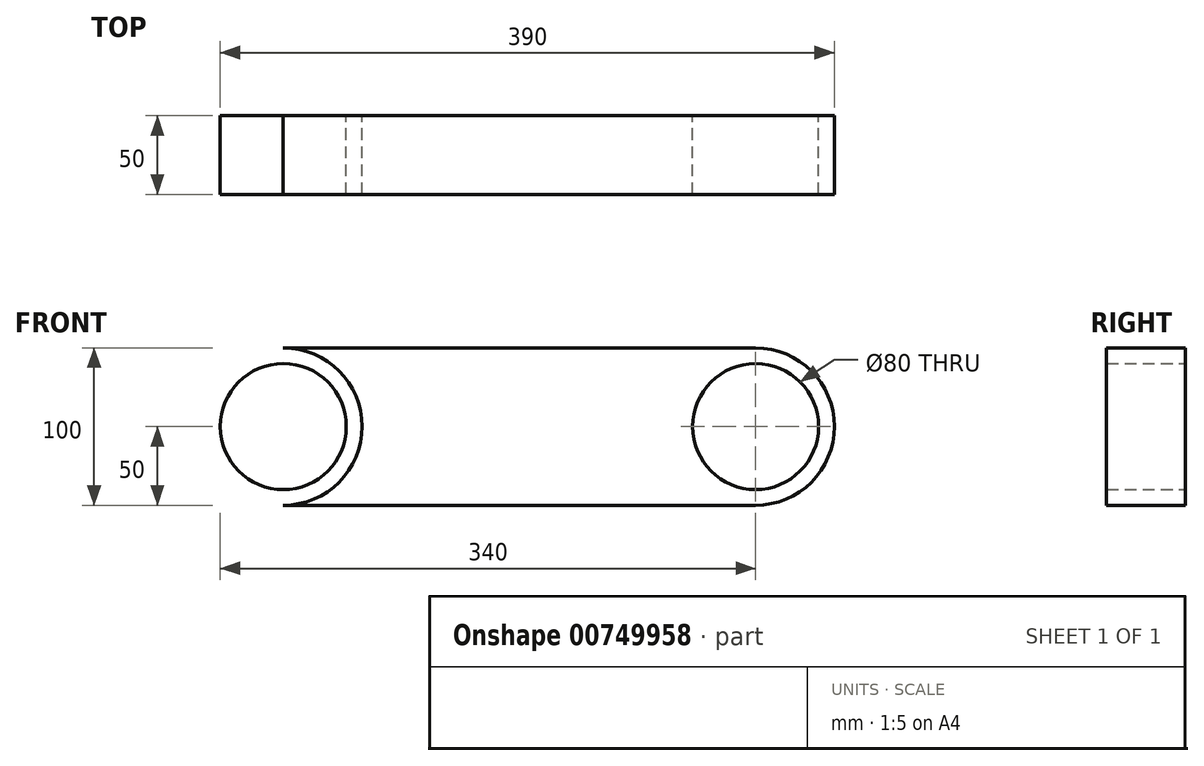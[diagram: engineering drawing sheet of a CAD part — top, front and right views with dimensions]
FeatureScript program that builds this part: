
annotation { "Feature Type Name" : "Feature", "Feature Type Description" : "" }
export const myFeature = defineFeature(function(context is Context, id is Id, definition is map)
    precondition{}
    {
        {
            var Q0;
            Q0=qCreatedBy(makeId("Front.planeOp"),FACE);
            var sketch = newSketch(context, id + "F0", { "sketchPlane" : qUnion([Q0])});
            skLineSegment(sketch, "E0.bottom", {"start": v(150, -50) * mm, "end": v(-150, -50) * mm});
            skLineSegment(sketch, "E0.top", {"start": v(150, 50) * mm, "end": v(-150, 50) * mm});
            skLineSegment(sketch, "E0.left", {"start": v(150, -50) * mm, "end": v(150, 50) * mm});
            skLineSegment(sketch, "E0.right", {"start": v(-150, -50) * mm, "end": v(-150, 50) * mm});
            skPoint(sketch, "E0.middle", {"position": v(0, 0) * mm});
            skCircle(sketch, "E1", {"center": v(150, 0) * mm, "radius": 50 * mm});
            skCircle(sketch, "E2.0", {"center": v(150, 0) * mm, "radius": 40 * mm});
            skLineSegment(sketch, "E3", {"start": v(0, 0) * mm, "end": v(0, -50) * mm});
            skCircle(sketch, "E4.MirrorC", {"center": v(-150, 0) * mm, "radius": 50 * mm});
            skCircle(sketch, "E5.MirrorC", {"center": v(-150, 0) * mm, "radius": 40 * mm});
            skSolve(sketch);
        }
        {
            var Q0;
            {var subQ4=sQuery(id+"F0.wireOp",EDGE,"E0.top");Q0=makeQuery(id+"F0.imprint","IMPRINT",FACE,{"disambiguationData":[TD([[makeQuery(id+"F0.imprint","IMPRINT",EDGE,{"derivedFrom":subQ4}),1.0]])]});}
            var Q1;
            {var subQ1=sQuery(id+"F0.wireOp",EDGE,"E0.right");var subQ3=sQuery(id+"F0.wireOp",EDGE,"E5.MirrorC");var subQ4=makeQuery(id+"F0.imprint","INTERSECT",VERTEX,{"disambiguationData":[OD(0.0)],"derivedFrom":[subQ1,subQ3]});Q1=makeQuery(id+"F0.imprint","IMPRINT",FACE,{"disambiguationData":[TD([[makeQuery(id+"F0.imprint","IMPRINT",EDGE,{"disambiguationData":[TD([[subQ4,1.0]])],"derivedFrom":subQ3}),1.0]])]});}
            var Q2;
            {var subQ1=sQuery(id+"F0.wireOp",EDGE,"E0.left");var subQ3=sQuery(id+"F0.wireOp",EDGE,"E2.0");var subQ4=makeQuery(id+"F0.imprint","INTERSECT",VERTEX,{"disambiguationData":[OD(0.0)],"derivedFrom":[subQ1,subQ3]});Q2=makeQuery(id+"F0.imprint","IMPRINT",FACE,{"disambiguationData":[TD([[makeQuery(id+"F0.imprint","IMPRINT",EDGE,{"disambiguationData":[TD([[subQ4,1.0]])],"derivedFrom":subQ3}),-1.0]])]});}
            var Q3;
            {var subQ1=sQuery(id+"F0.wireOp",EDGE,"E0.left");var subQ3=sQuery(id+"F0.wireOp",EDGE,"E2.0");var subQ4=makeQuery(id+"F0.imprint","INTERSECT",VERTEX,{"disambiguationData":[OD(0.0)],"derivedFrom":[subQ1,subQ3]});Q3=makeQuery(id+"F0.imprint","IMPRINT",FACE,{"disambiguationData":[TD([[makeQuery(id+"F0.imprint","IMPRINT",EDGE,{"disambiguationData":[TD([[subQ4,-1.0]])],"derivedFrom":subQ3}),-1.0]])]});}
            var Q4;
            {var subQ1=sQuery(id+"F0.wireOp",EDGE,"E0.right");var subQ3=sQuery(id+"F0.wireOp",EDGE,"E5.MirrorC");var subQ4=makeQuery(id+"F0.imprint","INTERSECT",VERTEX,{"disambiguationData":[OD(0.0)],"derivedFrom":[subQ1,subQ3]});Q4=makeQuery(id+"F0.imprint","IMPRINT",FACE,{"disambiguationData":[TD([[makeQuery(id+"F0.imprint","IMPRINT",EDGE,{"disambiguationData":[TD([[subQ4,-1.0]])],"derivedFrom":subQ3}),1.0]])]});}
            extrude(context, id + "F1", {"entities" : qUnion([Q0, Q1, Q2, Q3, Q4]), "depth" : 50 * mm, "offsetDistance" : 25 * mm});
        }
    });
